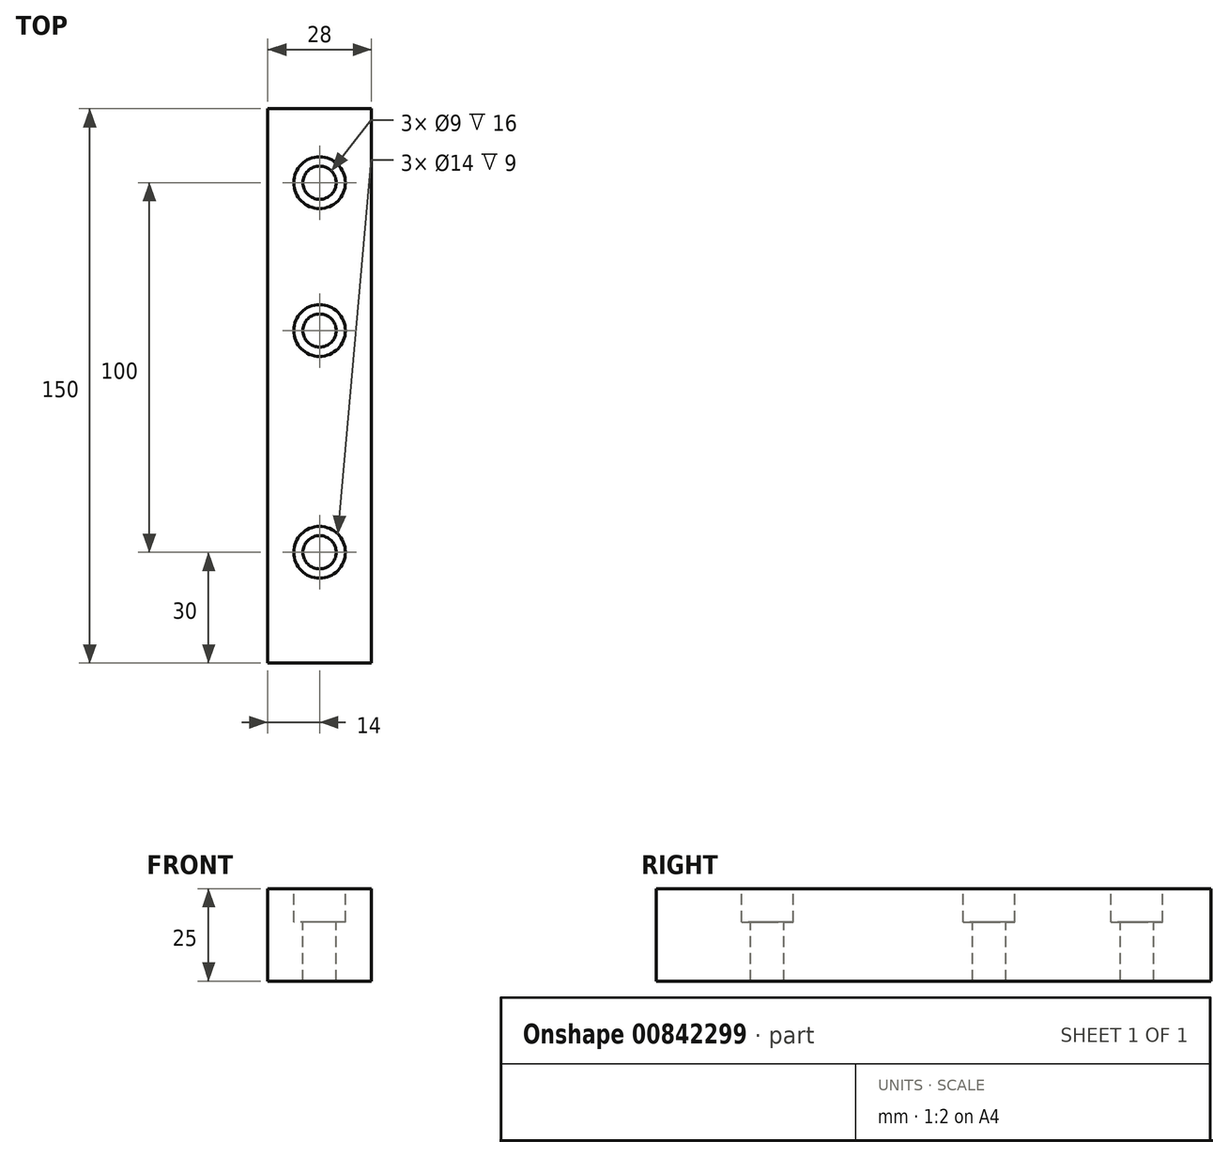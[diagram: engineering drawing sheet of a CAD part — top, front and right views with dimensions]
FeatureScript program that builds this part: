
annotation { "Feature Type Name" : "Feature", "Feature Type Description" : "" }
export const myFeature = defineFeature(function(context is Context, id is Id, definition is map)
    precondition{}
    {
        {
            var Q0;
            Q0=qCreatedBy(makeId("Front.planeOp"),FACE);
            var sketch = newSketch(context, id + "F0", { "sketchPlane" : qUnion([Q0])});
            skLineSegment(sketch, "E0.bottom", {"start": v(0, 0) * mm, "end": v(28, 0) * mm});
            skLineSegment(sketch, "E0.top", {"start": v(0, 25) * mm, "end": v(28, 25) * mm});
            skLineSegment(sketch, "E0.left", {"start": v(0, 0) * mm, "end": v(0, 25) * mm});
            skLineSegment(sketch, "E0.right", {"start": v(28, 0) * mm, "end": v(28, 25) * mm});
            skSolve(sketch);
        }
        {
            var Q0;
            Q0=makeQuery(id+"F0.imprint","IMPRINT",FACE,{"disambiguationData":[TD([[makeQuery(id+"F0.imprint","IMPRINT",EDGE,{"derivedFrom":sQuery(id+"F0.wireOp",EDGE,"E0.bottom")}),1.0]])]});
            extrude(context, id + "F1", {"entities" : qUnion([Q0]), "depth" : 150 * mm, "offsetDistance" : 25 * mm});
        }
        {
            var Q0;
            Q0=makeQuery(id+"F1.opExtrude","SWEPT_FACE",FACE,{"disambiguationData":[OSD([sQuery(id+"F0.wireOp",EDGE,"E0.top")])]});
            var sketch = newSketch(context, id + "F2", { "sketchPlane" : qUnion([Q0])});
            skPoint(sketch, "E1", {"position": v(14, -20) * mm});
            skPoint(sketch, "E2", {"position": v(14, -60) * mm});
            skPoint(sketch, "E3", {"position": v(14, -120) * mm});
            skSolve(sketch);
        }
        {
            var Q0;
            Q0=sQuery(id+"F2.wireOp",VERTEX,"E1");
            var Q1;
            Q1=sQuery(id+"F2.wireOp",VERTEX,"E2");
            var Q2;
            Q2=sQuery(id+"F2.wireOp",VERTEX,"E3");
            var Q3;
            Q3=makeQuery(id+"F1.opExtrude","SWEPT_BODY",BODY,{"disambiguationData":[OSD([sQuery(id+"F0.wireOp",EDGE,"E0.bottom"),sQuery(id+"F0.wireOp",EDGE,"E0.top"),sQuery(id+"F0.wireOp",EDGE,"E0.left"),sQuery(id+"F0.wireOp",EDGE,"E0.right")])]});
            hole(context, id + "F3", {"style" : HoleStyle.C_BORE, "endStyle" : HoleEndStyle.THROUGH, "holeDiameter" : 9 * mm, "cBoreDiameter" : 14 * mm, "cBoreDepth" : 9 * mm, "majorDiameter" : 5 * mm, "isTappedThrough" : true, "tappedDepth" : 12 * mm, "tapClearance" : 3, "locations" : qUnion([Q0, Q1, Q2]), "scope" : qUnion([Q3])});
        }
    });
